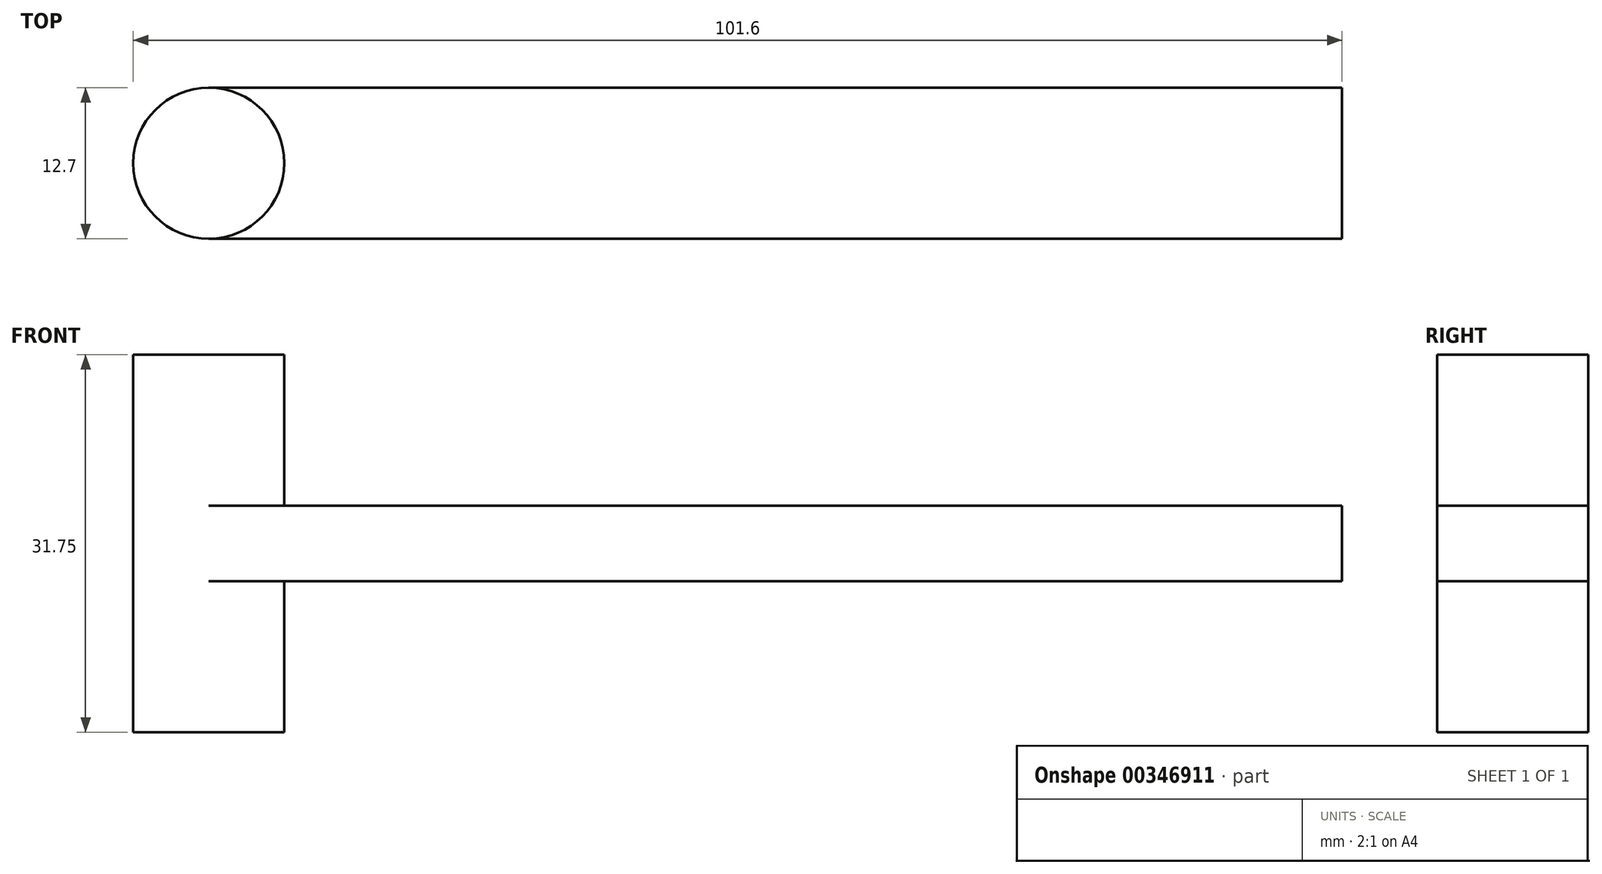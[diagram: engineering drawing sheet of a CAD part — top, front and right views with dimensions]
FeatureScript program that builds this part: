
annotation { "Feature Type Name" : "Feature", "Feature Type Description" : "" }
export const myFeature = defineFeature(function(context is Context, id is Id, definition is map)
    precondition{}
    {
        {
            var Q0;
            Q0=qCreatedBy(makeId("Top.planeOp"),FACE);
            var sketch = newSketch(context, id + "F0", { "sketchPlane" : qUnion([Q0])});
            skLineSegment(sketch, "E0.bottom", {"start": v(-50.8, 6.35) * mm, "end": v(76.2, 6.35) * mm});
            skLineSegment(sketch, "E0.top", {"start": v(-50.8, -6.35) * mm, "end": v(-27.64, -6.35) * mm});
            skLineSegment(sketch, "E0.left", {"start": v(-50.8, 6.35) * mm, "end": v(-50.8, -6.35) * mm});
            skLineSegment(sketch, "E0.right", {"start": v(50.8, 6.35) * mm, "end": v(50.8, -6.35) * mm});
            skPoint(sketch, "E0.middle", {"position": v(0, 0) * mm});
            skLineSegment(sketch, "E1.trimOffspring", {"start": v(101.6, 6.35) * mm, "end": v(101.6, 12.7) * mm});
            skPoint(sketch, "E2.right.start.orphan", {"position": v(193.68, -12.7) * mm});
            skLineSegment(sketch, "E3", {"start": v(-27.64, -6.35) * mm, "end": v(101.6, -6.35) * mm});
            skLineSegment(sketch, "E4", {"start": v(-27.64, 12.7) * mm, "end": v(-27.64, -6.35) * mm});
            skSolve(sketch);
        }
        {
            var Q0;
            Q0=makeQuery(id+"F0.imprint","IMPRINT",FACE,{"disambiguationData":[TD([[makeQuery(id+"F0.imprint","IMPRINT",EDGE,{"derivedFrom":sQuery(id+"F0.wireOp",EDGE,"E0.bottom")}),-1.0]])]});
            extrude(context, id + "F1", {"entities" : qUnion([Q0]), "depth" : 6.35 * mm});
        }
        {
            var Q0;
            Q0=makeQuery(id+"F1.opExtrude","CAP_FACE",FACE,{"disambiguationData":[OSD([sQuery(id+"F0.wireOp",EDGE,"E0.bottom"),sQuery(id+"F0.wireOp",EDGE,"E0.top"),sQuery(id+"F0.wireOp",EDGE,"E0.left"),sQuery(id+"F0.wireOp",EDGE,"E0.right"),sQuery(id+"F0.wireOp",EDGE,"E2.bottom"),sQuery(id+"F0.wireOp",EDGE,"E2.top"),sQuery(id+"F0.wireOp",EDGE,"E2.left"),sQuery(id+"F0.wireOp",EDGE,"E2.right"),sQuery(id+"F0.wireOp",EDGE,"E1.trimOffspring"),sQuery(id+"F0.wireOp",EDGE,"40e42468-3702-420b-9255-96b79e862e2b.trimOffspring")])],"isStart":true});
            var sketch = newSketch(context, id + "F2", { "sketchPlane" : qUnion([Q0])});
            skCircle(sketch, "E5", {"center": v(-44.45, 0) * mm, "radius": 6.35 * mm});
            skSolve(sketch);
        }
        {
            var Q0;
            {var subQ0=sQuery(id+"F2.wireOp",EDGE,"E5");var subQ1=makeQuery(id+"F2.imprint","INTERSECT",VERTEX,{"derivedFrom":[makeQuery(id+"F1.opExtrude","CAP_EDGE",EDGE,{"disambiguationData":[OSD([sQuery(id+"F0.wireOp",EDGE,"E0.left")])],"isStart":true}),subQ0]});Q0=makeQuery(id+"F2.imprint","IMPRINT",FACE,{"disambiguationData":[TD([[makeQuery(id+"F2.imprint","IMPRINT",EDGE,{"disambiguationData":[TD([[subQ1,1.0]])],"derivedFrom":subQ0}),1.0]])]});}
            extrude(context, id + "F3", {"entities" : qUnion([Q0]), "operationType" : NewBodyOperationType.ADD, "depth" : 12.7 * mm});
        }
        {
            var Q0;
            Q0=makeQuery(id+"F1.opExtrude","CAP_FACE",FACE,{"disambiguationData":[OSD([sQuery(id+"F0.wireOp",EDGE,"E0.bottom"),sQuery(id+"F0.wireOp",EDGE,"E0.top"),sQuery(id+"F0.wireOp",EDGE,"E0.left"),sQuery(id+"F0.wireOp",EDGE,"E0.right"),sQuery(id+"F0.wireOp",EDGE,"E2.bottom"),sQuery(id+"F0.wireOp",EDGE,"E2.top"),sQuery(id+"F0.wireOp",EDGE,"E2.left"),sQuery(id+"F0.wireOp",EDGE,"E2.right"),sQuery(id+"F0.wireOp",EDGE,"E1.trimOffspring"),sQuery(id+"F0.wireOp",EDGE,"40e42468-3702-420b-9255-96b79e862e2b.trimOffspring")])],"isStart":false});
            var sketch = newSketch(context, id + "F4", { "sketchPlane" : qUnion([Q0])});
            skCircle(sketch, "E6", {"center": v(-44.45, 0) * mm, "radius": 6.35 * mm});
            skSolve(sketch);
        }
        {
            var Q0;
            {var subQ0=sQuery(id+"F4.wireOp",EDGE,"E6");var subQ1=makeQuery(id+"F4.imprint","INTERSECT",VERTEX,{"derivedFrom":[makeQuery(id+"F1.opExtrude","CAP_EDGE",EDGE,{"disambiguationData":[OSD([sQuery(id+"F0.wireOp",EDGE,"E0.left")])],"isStart":false}),subQ0]});Q0=makeQuery(id+"F4.imprint","IMPRINT",FACE,{"disambiguationData":[TD([[makeQuery(id+"F4.imprint","IMPRINT",EDGE,{"disambiguationData":[TD([[subQ1,1.0]])],"derivedFrom":subQ0}),1.0]])]});}
            extrude(context, id + "F5", {"entities" : qUnion([Q0]), "operationType" : NewBodyOperationType.ADD, "depth" : 12.7 * mm});
        }
        {
            var Q0;
            Q0=makeQuery(id+"F1.opExtrude","SWEPT_EDGE",EDGE,{"disambiguationData":[OSD([sQuery(id+"F0.wireOp",EDGE,"E0.bottom"),sQuery(id+"F0.wireOp",EDGE,"E0.left")])]});
            fillet(context, id + "F6", {"entities" : qUnion([Q0]), "radius" : 6.35 * mm, "tangentPropagation" : true, "allowEdgeOverflow" : false});
        }
        {
            var Q0;
            Q0=makeQuery(id+"F1.opExtrude","SWEPT_EDGE",EDGE,{"disambiguationData":[OSD([sQuery(id+"F0.wireOp",EDGE,"E0.top"),sQuery(id+"F0.wireOp",EDGE,"E0.left")])]});
            fillet(context, id + "F7", {"entities" : qUnion([Q0]), "radius" : 6.35 * mm, "tangentPropagation" : true, "allowEdgeOverflow" : false});
        }
        {
            var Q0;
            {var subQ0=sQuery(id+"F0.wireOp",EDGE,"E3");var subQ1=sQuery(id+"F0.wireOp",EDGE,"E0.top");var subQ2=sQuery(id+"F0.wireOp",EDGE,"40e42468-3702-420b-9255-96b79e862e2b.trimOffspring");var subQ3=sQuery(id+"F0.wireOp",EDGE,"E1.trimOffspring");var subQ4=sQuery(id+"F0.wireOp",EDGE,"E2.top");var subQ5=sQuery(id+"F0.wireOp",EDGE,"E0.right");var subQ6=sQuery(id+"F0.wireOp",EDGE,"E0.bottom");var subQ7=makeQuery(id+"F1.opExtrude","CAP_FACE",FACE,{"disambiguationData":[OSD([subQ6,subQ1,sQuery(id+"F0.wireOp",EDGE,"E0.left"),subQ5,subQ4,subQ3,subQ2,subQ0])],"isStart":false});Q0=makeQuery(id+"F5.boolean.opBoolean","SPLIT",FACE,{"disambiguationData":[TD([makeQuery(id+"F1.opExtrude","SWEPT_FACE",FACE,{"disambiguationData":[OSD([subQ6])]}),subQ7,makeQuery(id+"F1.opExtrude","SWEPT_FACE",FACE,{"disambiguationData":[OSD([subQ1,subQ0])]}),makeQuery(id+"F1.opExtrude","SWEPT_FACE",FACE,{"disambiguationData":[OSD([subQ5,subQ3])]}),makeQuery(id+"F1.opExtrude","SWEPT_FACE",FACE,{"disambiguationData":[OSD([subQ4])]}),makeQuery(id+"F1.opExtrude","SWEPT_FACE",FACE,{"disambiguationData":[OSD([subQ2])]}),makeQuery(id+"F5.opExtrude","SWEPT_FACE",FACE,{"disambiguationData":[OSD([sQuery(id+"F4.wireOp",EDGE,"E6")])]})])],"derivedFrom":subQ7});}
            var sketch = newSketch(context, id + "F8", { "sketchPlane" : qUnion([Q0])});
            skCircle(sketch, "E7", {"center": v(63.46, 1.05) * mm, "radius": 6.35 * mm});
            skSolve(sketch);
        }
        {
            var Q0;
            Q0=makeQuery(id+"F8.imprint","IMPRINT",FACE,{"disambiguationData":[TD([[makeQuery(id+"F8.imprint","IMPRINT",EDGE,{"derivedFrom":sQuery(id+"F8.wireOp",EDGE,"E7")}),1.0]])]});
            extrude(context, id + "F9", {"entities" : qUnion([Q0]), "operationType" : NewBodyOperationType.REMOVE, "oppositeDirection" : true, "depth" : 25.4 * mm});
        }
    });
